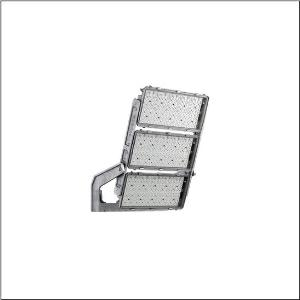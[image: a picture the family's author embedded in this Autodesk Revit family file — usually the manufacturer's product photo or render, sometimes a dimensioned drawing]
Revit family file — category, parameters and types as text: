
# Revit family: floodlight_fl_11_maxi_pro_remote___pl64_5xa779524e01aa_eec4
name_source: partatom
category: Lighting Fixtures
units: mm (PartAtom-declared; Revit-internal decimal feet)

## family parameters
Cut with Voids When Loaded = No
Host = Face
Light Source = No
Part Type = Normal
Room Calculation Point = No
Round Connector Dimension = Use Diameter
Shared = No

## types (1)
- --- (1 x LED, 128450 lm, 1334.7 W, 5700K)
    Apparent Load = 1335 VA
    CIE Flux Codes = 28 80 98 100 100
    Color Rendering = 90
    Color Temperature = 5700K
    Default Elevation = 1800 mm
    Description = Floodlight FL 11  maxi  pro Remote floodlight; light control with lens of PMMA; cover panel of toughened safety glass, transparent; light distribution: PL64, asymmetric direct distribution, LEDcolour temperature: 5700K, rated luminous flux: 128.450lm, colour rendering: CRI > 90, light colour: 957; luminous efficacy: 96lm/W; brightness control: DMX+RDM; with terminal, 6-pole, max. 2.5mm², mains connection: 220..240V/380..400V AC, 50/60Hz, surge voltage resistance: line to ground: 10kV, ECG replaceable separately, no afterglow with DALI off / DMX off command, LED unit replaceable without ESD environment, dustproof LED module, dimming range 10..100%; 1335W floodlight with 3x LED unit of diecast aluminium, coated grey; length: 713mm / width: 651mm / height: 338mm; mounting bracket, of diecast aluminium, uncoated, natural, equipment: Power, protection rating (complete): IP66; insulation class (complete): insulation class I (protective earthing); certification: CE, ENEC, VDE; ball protection: ball impact resistance with accessories, impact resistance: IK07; only for outdoor installations, rated ambient temperature 10°C, permissible operating ambient temperature: -40..+30°C, permissible storage temperature: -40..+85°C; packaging unit: 1 piece

Light Distribution: PL64
    Height = 320 mm
    Lamp = 1 x LED
    Lamp Light Flux = 128450 lm
    Lamp Power = 1334.7 W
    Lamp count = 1
    Length = 1002 mm
    Luminous efficacy = 96 lm/W
    Manufacturer = Siteco
    ModVariant = No
    Model = 5XA779524E01AA
    Mounting Place = Ceiling
    Mounting Type = Surface mounted
    Number of Poles = 1
    OnlyDefault = Yes
    Power Factor = 1
    Product Name = Floodlight FL 11 maxi pro Remote | PL64
    Product group = floodlight | ceiling mounted
    ProductGroupID = 302
    Protection Class = Protection class I
    Protection Degree = IP 66
    RLX_Detail_Level = 1
    RLX_Emergency_Light_Flux = 0 lm
    RLX_Emergency_Type = 0
    RLX_Emergency_Type_DB = No
    RlxData = <blob elided: 52345 chars, md5=78fed845>
    Socket = socket
    Standby Power = 0 W
    System Light Flux = 128450 lm
    System Power = 1335 W
    Type Comments = factory setting: luminous flux: 100 % | dim-lin: 255 | 920 mA
    Type Image = l_1006784.jpg
    URL = http://relux.com
    VarID = @adj_027603
    Voltage = 0 V
    Weight = 0.00 kg
    Width = 655 mm

## geometry (parser evidence)
native form markers: Blend x4, Sweep x13
no freeform markers — native parametric forms only
